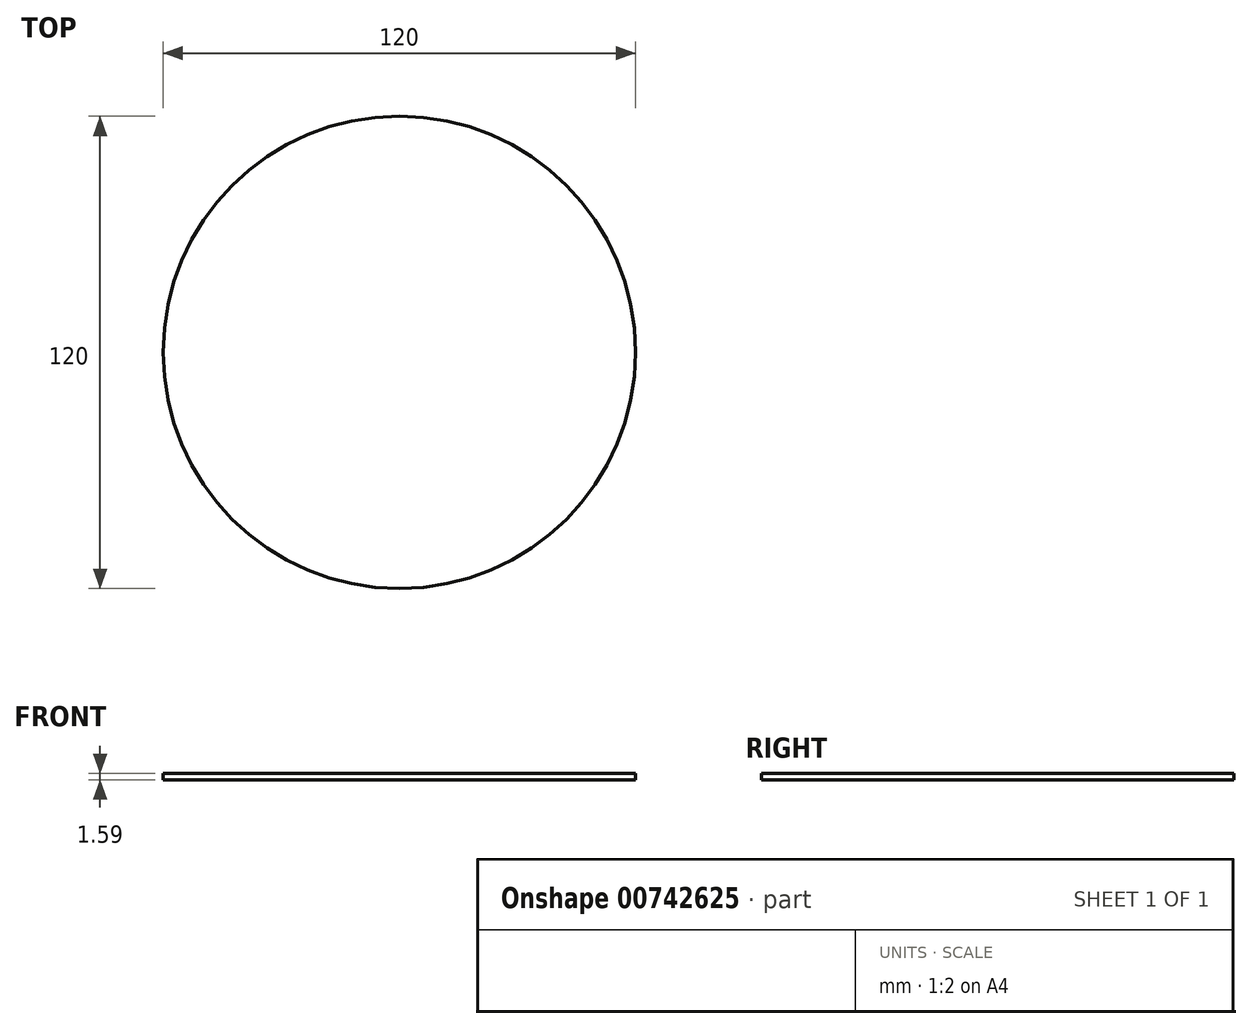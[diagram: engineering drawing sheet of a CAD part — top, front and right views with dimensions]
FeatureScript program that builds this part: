
annotation { "Feature Type Name" : "Feature", "Feature Type Description" : "" }
export const myFeature = defineFeature(function(context is Context, id is Id, definition is map)
    precondition{}
    {
        {
            var Q0;
            Q0=qCreatedBy(makeId("Top.planeOp"),FACE);
            var sketch = newSketch(context, id + "F0", { "sketchPlane" : qUnion([Q0])});
            skCircle(sketch, "E0", {"center": v(0, 0) * mm, "radius": 60 * mm});
            skSolve(sketch);
        }
        {
            var Q0;
            Q0=makeQuery(id+"F0.imprint","IMPRINT",FACE,{"disambiguationData":[TD([[makeQuery(id+"F0.imprint","IMPRINT",EDGE,{"derivedFrom":sQuery(id+"F0.wireOp",EDGE,"E0")}),1.0]])]});
            extrude(context, id + "F1", {"entities" : qUnion([Q0]), "depth" : 1.59 * mm, "offsetDistance" : 25.4 * mm});
        }
    });
